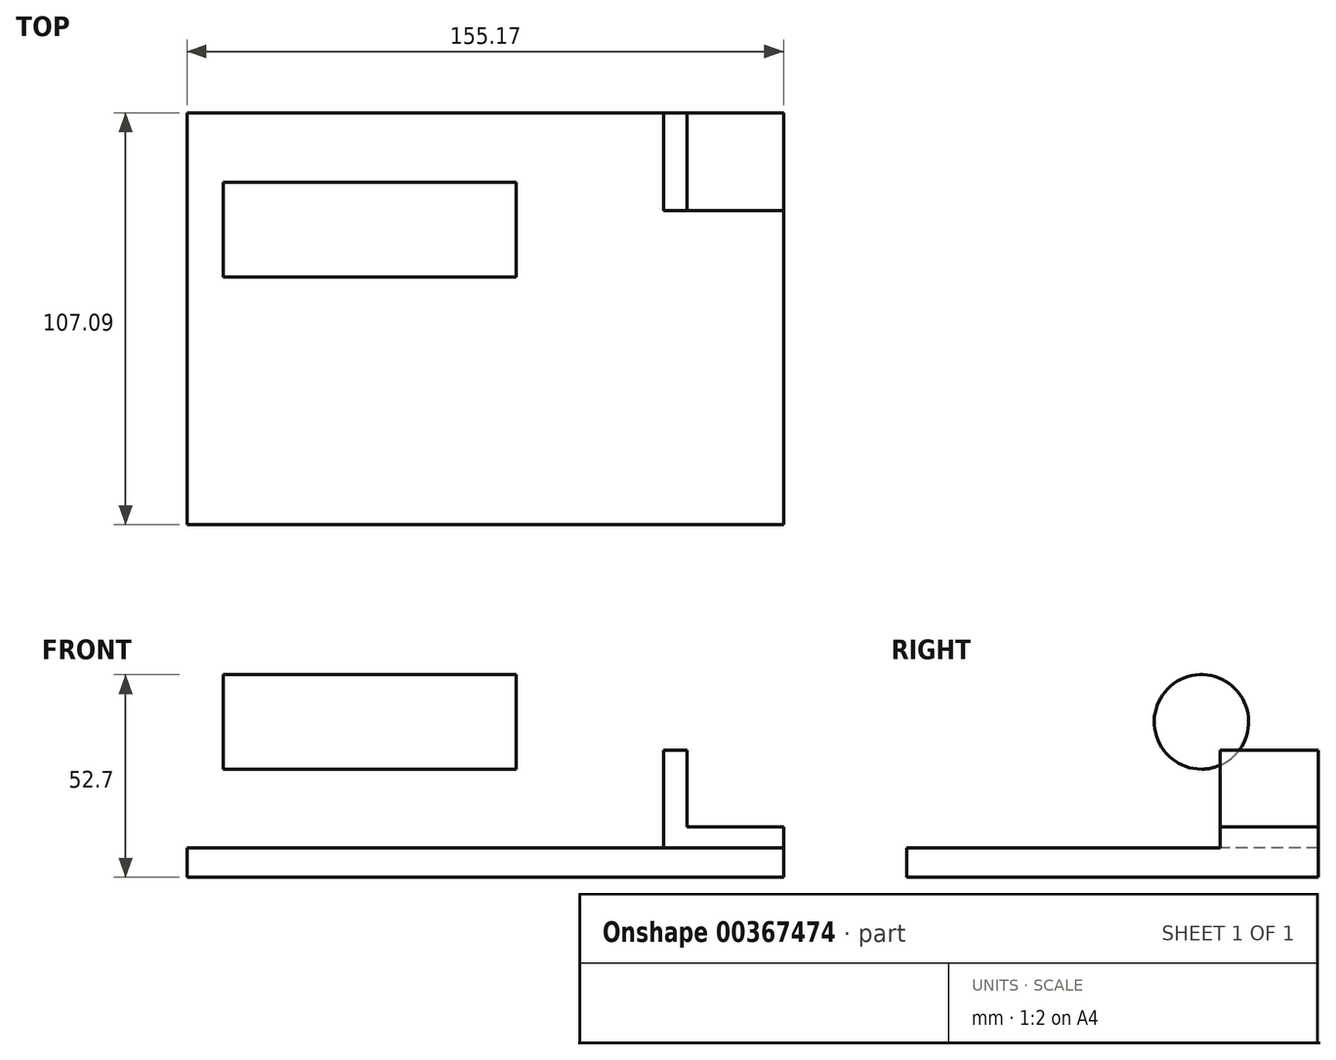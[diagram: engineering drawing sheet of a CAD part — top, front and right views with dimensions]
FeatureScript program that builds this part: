
annotation { "Feature Type Name" : "Feature", "Feature Type Description" : "" }
export const myFeature = defineFeature(function(context is Context, id is Id, definition is map)
    precondition{}
    {
        {
            var Q0;
            Q0=qCreatedBy(makeId("Top.planeOp"),FACE);
            var sketch = newSketch(context, id + "F0", { "sketchPlane" : qUnion([Q0])});
            skLineSegment(sketch, "E0.bottom", {"start": v(-85.57, 57.27) * mm, "end": v(69.6, 57.27) * mm});
            skLineSegment(sketch, "E0.top", {"start": v(-85.57, -49.82) * mm, "end": v(69.6, -49.82) * mm});
            skLineSegment(sketch, "E0.left", {"start": v(-85.57, 57.27) * mm, "end": v(-85.57, -49.82) * mm});
            skLineSegment(sketch, "E0.right", {"start": v(69.6, 57.27) * mm, "end": v(69.6, -49.82) * mm});
            skSolve(sketch);
        }
        {
            var Q0;
            Q0 = qSketchRegion(id + "F0", true);
            extrude(context, id + "F1", {"entities" : qUnion([Q0]), "depth" : 7.62 * mm});
        }
        {
            var Q0;
            Q0=makeQuery(id+"F1.opExtrude","CAP_FACE",FACE,{"disambiguationData":[OSD([sQuery(id+"F0.wireOp",EDGE,"E0.bottom"),sQuery(id+"F0.wireOp",EDGE,"E0.top"),sQuery(id+"F0.wireOp",EDGE,"E0.left"),sQuery(id+"F0.wireOp",EDGE,"E0.right")])],"isStart":false});
            var sketch = newSketch(context, id + "F2", { "sketchPlane" : qUnion([Q0])});
            skLineSegment(sketch, "E1.bottom", {"start": v(44.52, 57.27) * mm, "end": v(69.6, 57.27) * mm});
            skLineSegment(sketch, "E1.top", {"start": v(44.52, 31.8) * mm, "end": v(69.6, 31.8) * mm});
            skLineSegment(sketch, "E1.left", {"start": v(44.52, 57.27) * mm, "end": v(44.52, 31.8) * mm});
            skLineSegment(sketch, "E1.right", {"start": v(69.6, 57.27) * mm, "end": v(69.6, 31.8) * mm});
            skSolve(sketch);
        }
        {
            var Q0;
            Q0 = qSketchRegion(id + "F2", true);
            extrude(context, id + "F3", {"entities" : qUnion([Q0]), "operationType" : NewBodyOperationType.ADD, "depth" : 5.46 * mm});
        }
        {
            var Q0;
            Q0=makeQuery(id+"F1.opExtrude","CAP_FACE",FACE,{"disambiguationData":[OSD([sQuery(id+"F0.wireOp",EDGE,"E0.bottom"),sQuery(id+"F0.wireOp",EDGE,"E0.top"),sQuery(id+"F0.wireOp",EDGE,"E0.left"),sQuery(id+"F0.wireOp",EDGE,"E0.right")])],"isStart":false});
            var sketch = newSketch(context, id + "F4", { "sketchPlane" : qUnion([Q0])});
            skLineSegment(sketch, "E2.bottom", {"start": v(38.42, 57.27) * mm, "end": v(44.52, 57.27) * mm});
            skLineSegment(sketch, "E2.top", {"start": v(38.42, 31.8) * mm, "end": v(44.52, 31.8) * mm});
            skLineSegment(sketch, "E2.left", {"start": v(38.42, 57.27) * mm, "end": v(38.42, 31.8) * mm});
            skLineSegment(sketch, "E2.right", {"start": v(44.52, 57.27) * mm, "end": v(44.52, 31.8) * mm});
            skSolve(sketch);
        }
        {
            var Q0;
            Q0 = qSketchRegion(id + "F4", true);
            extrude(context, id + "F5", {"entities" : qUnion([Q0]), "operationType" : NewBodyOperationType.ADD, "depth" : 25.4 * mm});
        }
        {
            var Q0;
            Q0=qCreatedBy(makeId("Right.planeOp"),FACE);
            var sketch = newSketch(context, id + "F6", { "sketchPlane" : qUnion([Q0])});
            skCircle(sketch, "E3", {"center": v(26.88, 40.42) * mm, "radius": 12.29 * mm});
            skSolve(sketch);
        }
        {
            var Q0;
            Q0 = qSketchRegion(id + "F6", true);
            extrude(context, id + "F7", {"entities" : qUnion([Q0]), "oppositeDirection" : true, "depth" : 76.2 * mm});
        }
    });
